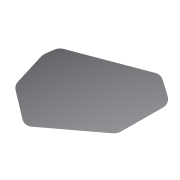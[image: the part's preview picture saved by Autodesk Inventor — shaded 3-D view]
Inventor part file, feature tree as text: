
AUTODESK INVENTOR PART (.ipt)
format: ipt  version: 2020 (Build 240168000, 168)  size: 193,536 bytes
history: native  units: mm
features: other x6, fillet x2, imported_body x1, extrude x1
ambient origin geometry x8: Origin, YZ Plane, XZ Plane, XY Plane, X Axis, Y Axis, Z Axis, Center Point
bodies: Body1 (feature_tree)
feature tree (10):
  imported_body  "Base"
  extrude  "BaseFeature"  Depth=25.481807mm
  fillet  "SmallFilletsFeature"  Radius=18.849556mm
  fillet  "LargeFilletsFeature"  Radius=21.642083mm
  other  "SlopeProfileMiddlePlane"
  other  "SlopeProfileIntersect"
  other  "SlopeProfileIntersectFeature"
  other  "SlopeProfileSubtractFeature"
  other  "SlopeProfilePlane"
  other  "SlopeProfileSubtract"
